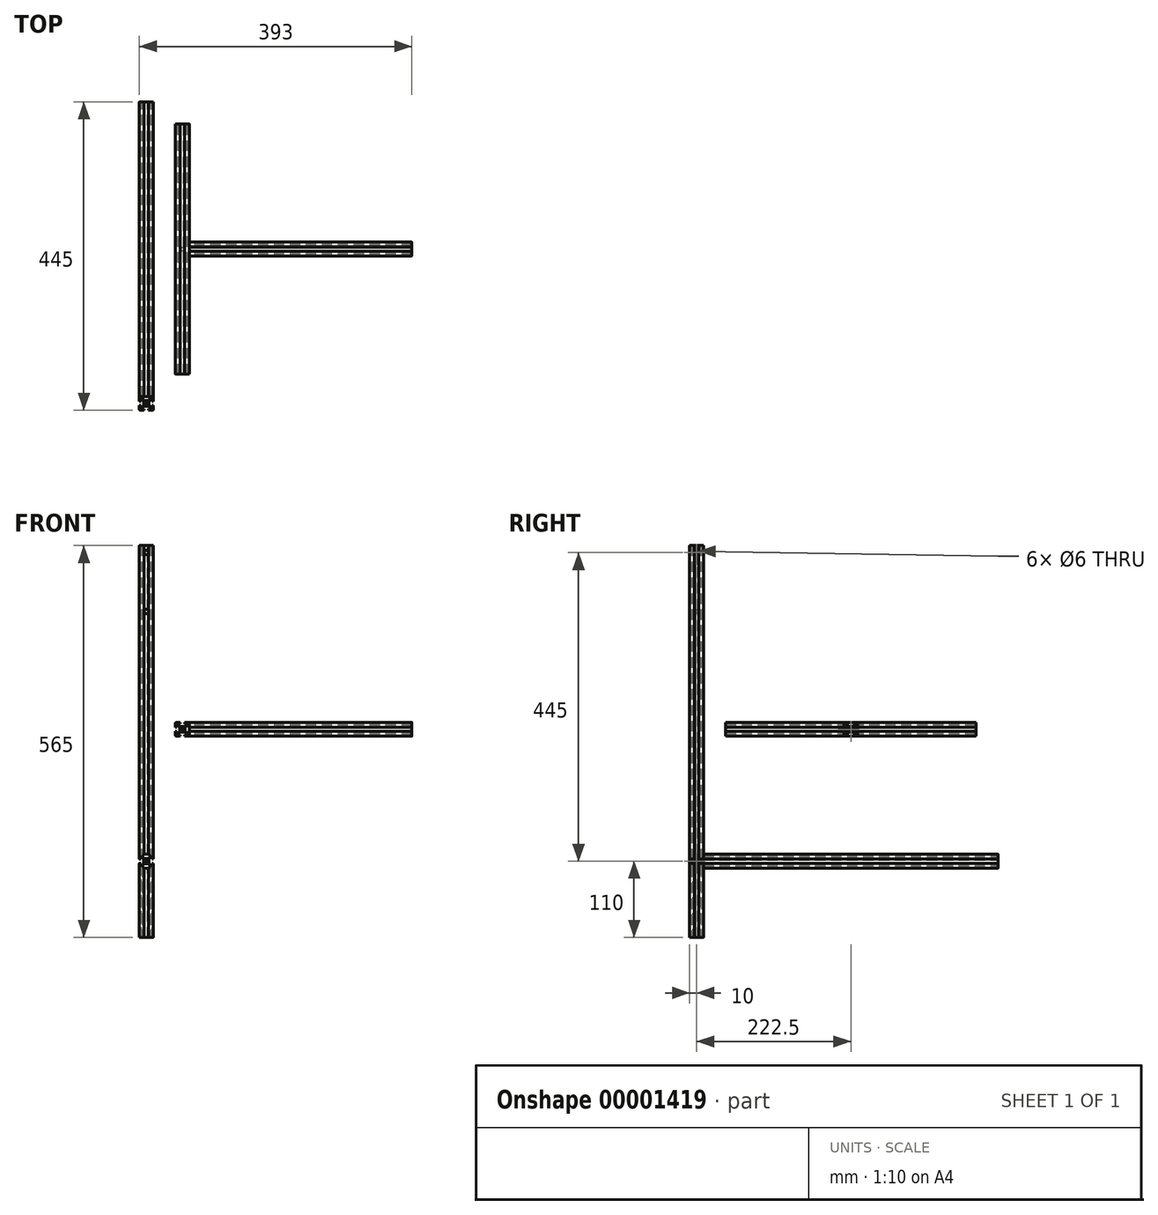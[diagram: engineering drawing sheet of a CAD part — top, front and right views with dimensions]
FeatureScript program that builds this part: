
annotation { "Feature Type Name" : "Feature", "Feature Type Description" : "" }
export const myFeature = defineFeature(function(context is Context, id is Id, definition is map)
    precondition{}
    {
        {
            var Q0;
            Q0=qCreatedBy(makeId("Top.planeOp"),FACE);
            cPlane(context, id + "F0", {"entities" : qUnion([Q0]), "cplaneType" : CPlaneType.OFFSET, "offset" : 565 * mm, "width" : 150 * mm, "height" : 150 * mm});
        }
        {
            var Q0;
            Q0=qCreatedBy(makeId("Top.planeOp"),FACE);
            var sketch = newSketch(context, id + "F1", { "sketchPlane" : qUnion([Q0])});
            skLineSegment(sketch, "E0", {"start": v(0, 0) * mm, "end": v(-232.5, 0) * mm, "construction": true});
            skLineSegment(sketch, "E1", {"start": v(0, 0) * mm, "end": v(0, -232.5) * mm, "construction": true});
            skLineSegment(sketch, "E2", {"start": v(0, -212.5) * mm, "end": v(-212.5, -212.5) * mm, "construction": true});
            skLineSegment(sketch, "E3", {"start": v(-212.5, -212.5) * mm, "end": v(-212.5, 0) * mm, "construction": true});
            skLineSegment(sketch, "E4", {"start": v(-232.5, 0) * mm, "end": v(-232.5, -212.5) * mm, "construction": true});
            skLineSegment(sketch, "E5", {"start": v(-232.5, -212.5) * mm, "end": v(-232.5, -232.5) * mm, "construction": true});
            skLineSegment(sketch, "E6", {"start": v(-232.5, -232.5) * mm, "end": v(-212.5, -232.5) * mm, "construction": true});
            skLineSegment(sketch, "E7", {"start": v(-212.5, -232.5) * mm, "end": v(0, -232.5) * mm, "construction": true});
            skLineSegment(sketch, "E8", {"start": v(-232.5, -212.5) * mm, "end": v(-212.5, -212.5) * mm, "construction": true});
            skLineSegment(sketch, "E9", {"start": v(-212.5, -232.5) * mm, "end": v(-212.5, -212.5) * mm, "construction": true});
            skLineSegment(sketch, "E10.0.MirrorCS", {"start": v(-212.5, 212.5) * mm, "end": v(-212.5, 0) * mm, "construction": true});
            skLineSegment(sketch, "E10.1.MirrorCS", {"start": v(-232.5, 0) * mm, "end": v(-232.5, 212.5) * mm, "construction": true});
            skLineSegment(sketch, "E10.2.MirrorCS", {"start": v(0, 212.5) * mm, "end": v(-212.5, 212.5) * mm, "construction": true});
            skLineSegment(sketch, "E10.3.MirrorCS", {"start": v(-212.5, 232.5) * mm, "end": v(0, 232.5) * mm, "construction": true});
            skLineSegment(sketch, "E10.4.MirrorCS", {"start": v(-232.5, 212.5) * mm, "end": v(-232.5, 232.5) * mm, "construction": true});
            skLineSegment(sketch, "E10.5.MirrorCS", {"start": v(-212.5, 232.5) * mm, "end": v(-212.5, 212.5) * mm, "construction": true});
            skLineSegment(sketch, "E10.6.MirrorCS", {"start": v(-232.5, 232.5) * mm, "end": v(-212.5, 232.5) * mm, "construction": true});
            skLineSegment(sketch, "E10.7.MirrorCS", {"start": v(-232.5, 212.5) * mm, "end": v(-212.5, 212.5) * mm, "construction": true});
            skLineSegment(sketch, "E11.0.MirrorCS", {"start": v(232.5, 232.5) * mm, "end": v(212.5, 232.5) * mm, "construction": true});
            skLineSegment(sketch, "E11.1.MirrorCS", {"start": v(232.5, 212.5) * mm, "end": v(232.5, 232.5) * mm, "construction": true});
            skLineSegment(sketch, "E11.2.MirrorCS", {"start": v(212.5, 232.5) * mm, "end": v(212.5, 212.5) * mm, "construction": true});
            skLineSegment(sketch, "E11.3.MirrorCS", {"start": v(232.5, 212.5) * mm, "end": v(212.5, 212.5) * mm, "construction": true});
            skLineSegment(sketch, "E11.4.MirrorCS", {"start": v(212.5, 232.5) * mm, "end": v(0, 232.5) * mm, "construction": true});
            skLineSegment(sketch, "E11.5.MirrorCS", {"start": v(0, 212.5) * mm, "end": v(212.5, 212.5) * mm, "construction": true});
            skLineSegment(sketch, "E11.6.MirrorCS", {"start": v(232.5, 0) * mm, "end": v(232.5, 212.5) * mm, "construction": true});
            skLineSegment(sketch, "E11.7.MirrorCS", {"start": v(212.5, 212.5) * mm, "end": v(212.5, 0) * mm, "construction": true});
            skLineSegment(sketch, "E11.8.MirrorCS", {"start": v(232.5, 0) * mm, "end": v(232.5, -212.5) * mm, "construction": true});
            skLineSegment(sketch, "E11.9.MirrorCS", {"start": v(212.5, -212.5) * mm, "end": v(212.5, 0) * mm, "construction": true});
            skLineSegment(sketch, "E11.10.MirrorCS", {"start": v(0, -212.5) * mm, "end": v(212.5, -212.5) * mm, "construction": true});
            skLineSegment(sketch, "E11.11.MirrorCS", {"start": v(212.5, -232.5) * mm, "end": v(0, -232.5) * mm, "construction": true});
            skLineSegment(sketch, "E11.12.MirrorCS", {"start": v(232.5, -232.5) * mm, "end": v(212.5, -232.5) * mm, "construction": true});
            skLineSegment(sketch, "E11.13.MirrorCS", {"start": v(232.5, -212.5) * mm, "end": v(232.5, -232.5) * mm, "construction": true});
            skLineSegment(sketch, "E11.14.MirrorCS", {"start": v(232.5, -212.5) * mm, "end": v(212.5, -212.5) * mm, "construction": true});
            skLineSegment(sketch, "E11.15.MirrorCS", {"start": v(212.5, -232.5) * mm, "end": v(212.5, -212.5) * mm, "construction": true});
            skLineSegment(sketch, "E12.0.MirrorCS", {"start": v(0, 0) * mm, "end": v(232.5, 0) * mm, "construction": true});
            skLineSegment(sketch, "E13.0.MirrorCS", {"start": v(0, 0) * mm, "end": v(0, 232.5) * mm, "construction": true});
            skSolve(sketch);
        }
        {
            var Q0;
            Q0=sQuery(id+"F1.wireOp",EDGE,"E13.0.MirrorCS");
            var Q1;
            Q1=sQuery(id+"F1.wireOp",VERTEX,"E10.2.MirrorCS.start");
            cPlane(context, id + "F2", {"entities" : qUnion([Q0, Q1]), "cplaneType" : CPlaneType.LINE_POINT, "offset" : 150 * mm, "width" : 150 * mm, "height" : 150 * mm});
        }
        {
            var Q0;
            Q0=qCreatedBy(makeId("Right.planeOp"),FACE);
            var sketch = newSketch(context, id + "F3", { "sketchPlane" : qUnion([Q0])});
            skLineSegment(sketch, "E14.rect.bottom", {"start": v(10, 10) * mm, "end": v(3, 10) * mm});
            skLineSegment(sketch, "E14.rect.top", {"start": v(10, -10) * mm, "end": v(3, -10) * mm});
            skLineSegment(sketch, "E14.rect.left", {"start": v(10, 10) * mm, "end": v(10, 3) * mm});
            skLineSegment(sketch, "E14.rect.right", {"start": v(-10, 10) * mm, "end": v(-10, 3) * mm});
            skPoint(sketch, "E14.rect.middle", {"position": v(0, 0) * mm});
            skLineSegment(sketch, "E15", {"start": v(-3, 10) * mm, "end": v(-3, 8) * mm});
            skLineSegment(sketch, "E16", {"start": v(-3, 8) * mm, "end": v(-6, 8) * mm});
            skLineSegment(sketch, "E17", {"start": v(-6, 8) * mm, "end": v(-6, 7.06) * mm});
            skLineSegment(sketch, "E18", {"start": v(-6, 7.06) * mm, "end": v(-2.94, 4) * mm});
            skLineSegment(sketch, "E19", {"start": v(-2.94, 4) * mm, "end": v(2.94, 4) * mm});
            skLineSegment(sketch, "E20", {"start": v(2.94, 4) * mm, "end": v(6, 7.06) * mm});
            skLineSegment(sketch, "E21", {"start": v(6, 7.06) * mm, "end": v(6, 8) * mm});
            skLineSegment(sketch, "E22", {"start": v(6, 8) * mm, "end": v(3, 8) * mm});
            skLineSegment(sketch, "E23", {"start": v(3, 8) * mm, "end": v(3, 10) * mm});
            skLineSegment(sketch, "E24.trimOffspring", {"start": v(-3, 10) * mm, "end": v(-10, 10) * mm});
            skLineSegment(sketch, "E25", {"start": v(10, 3) * mm, "end": v(8, 3) * mm});
            skLineSegment(sketch, "E26", {"start": v(8, 3) * mm, "end": v(8, 6) * mm});
            skLineSegment(sketch, "E27", {"start": v(8, 6) * mm, "end": v(7.06, 6) * mm});
            skLineSegment(sketch, "E28", {"start": v(7.06, 6) * mm, "end": v(4, 2.94) * mm});
            skLineSegment(sketch, "E29", {"start": v(4, 2.94) * mm, "end": v(4, -2.94) * mm});
            skLineSegment(sketch, "E30", {"start": v(4, -2.94) * mm, "end": v(7.06, -6) * mm});
            skLineSegment(sketch, "E31", {"start": v(7.06, -6) * mm, "end": v(8, -6) * mm});
            skLineSegment(sketch, "E32", {"start": v(8, -6) * mm, "end": v(8, -3) * mm});
            skLineSegment(sketch, "E33", {"start": v(8, -3) * mm, "end": v(10, -3) * mm});
            skLineSegment(sketch, "E34.trimOffspring", {"start": v(10, -3) * mm, "end": v(10, -10) * mm});
            skLineSegment(sketch, "E35", {"start": v(3, -10) * mm, "end": v(3, -8) * mm});
            skLineSegment(sketch, "E36", {"start": v(3, -8) * mm, "end": v(6, -8) * mm});
            skLineSegment(sketch, "E37", {"start": v(6, -8) * mm, "end": v(6, -7.06) * mm});
            skLineSegment(sketch, "E38", {"start": v(6, -7.06) * mm, "end": v(2.94, -4) * mm});
            skLineSegment(sketch, "E39", {"start": v(2.94, -4) * mm, "end": v(-2.94, -4) * mm});
            skLineSegment(sketch, "E40", {"start": v(-2.94, -4) * mm, "end": v(-6, -7.06) * mm});
            skLineSegment(sketch, "E41", {"start": v(-6, -7.06) * mm, "end": v(-6, -8) * mm});
            skLineSegment(sketch, "E42", {"start": v(-6, -8) * mm, "end": v(-3, -8) * mm});
            skLineSegment(sketch, "E43", {"start": v(-3, -8) * mm, "end": v(-3, -10) * mm});
            skLineSegment(sketch, "E44", {"start": v(-10, -3) * mm, "end": v(-8, -3) * mm});
            skLineSegment(sketch, "E45", {"start": v(-8, -3) * mm, "end": v(-8, -6) * mm});
            skLineSegment(sketch, "E46", {"start": v(-8, -6) * mm, "end": v(-7.06, -6) * mm});
            skLineSegment(sketch, "E47", {"start": v(-7.06, -6) * mm, "end": v(-4, -2.94) * mm});
            skLineSegment(sketch, "E48", {"start": v(-4, -2.94) * mm, "end": v(-4, 2.94) * mm});
            skLineSegment(sketch, "E49", {"start": v(-4, 2.94) * mm, "end": v(-7.06, 6) * mm});
            skLineSegment(sketch, "E50", {"start": v(-7.06, 6) * mm, "end": v(-8, 6) * mm});
            skLineSegment(sketch, "E51", {"start": v(-8, 6) * mm, "end": v(-8, 3) * mm});
            skLineSegment(sketch, "E52", {"start": v(-8, 3) * mm, "end": v(-10, 3) * mm});
            skLineSegment(sketch, "E53.trimOffspring", {"start": v(-3, -10) * mm, "end": v(-10, -10) * mm});
            skLineSegment(sketch, "E54.trimOffspring", {"start": v(-10, -3) * mm, "end": v(-10, -10) * mm});
            skSolve(sketch);
        }
        {
            var Q0;
            Q0=makeQuery(id+"F3.imprint","IMPRINT",FACE,{"disambiguationData":[TD([[makeQuery(id+"F3.imprint","IMPRINT",EDGE,{"derivedFrom":sQuery(id+"F3.wireOp",EDGE,"E14.rect.bottom")}),1.0]])]});
            extrude(context, id + "F4", {"entities" : qUnion([Q0]), "depth" : 321 * mm, "symmetric" : true});
        }
        {
            var Q0;
            Q0=makeQuery(id+"F4.opExtrude","CAP_FACE",FACE,{"disambiguationData":[OSD([sQuery(id+"F3.wireOp",EDGE,"E14.rect.bottom"),sQuery(id+"F3.wireOp",EDGE,"E14.rect.top"),sQuery(id+"F3.wireOp",EDGE,"E14.rect.left"),sQuery(id+"F3.wireOp",EDGE,"E14.rect.right"),sQuery(id+"F3.wireOp",EDGE,"E15"),sQuery(id+"F3.wireOp",EDGE,"E16"),sQuery(id+"F3.wireOp",EDGE,"E17"),sQuery(id+"F3.wireOp",EDGE,"E18"),sQuery(id+"F3.wireOp",EDGE,"E19"),sQuery(id+"F3.wireOp",EDGE,"E20"),sQuery(id+"F3.wireOp",EDGE,"E21"),sQuery(id+"F3.wireOp",EDGE,"E22"),sQuery(id+"F3.wireOp",EDGE,"E23"),sQuery(id+"F3.wireOp",EDGE,"E24.trimOffspring"),sQuery(id+"F3.wireOp",EDGE,"E25"),sQuery(id+"F3.wireOp",EDGE,"E26"),sQuery(id+"F3.wireOp",EDGE,"E27"),sQuery(id+"F3.wireOp",EDGE,"E28"),sQuery(id+"F3.wireOp",EDGE,"E29"),sQuery(id+"F3.wireOp",EDGE,"E30"),sQuery(id+"F3.wireOp",EDGE,"E31"),sQuery(id+"F3.wireOp",EDGE,"E32"),sQuery(id+"F3.wireOp",EDGE,"E33"),sQuery(id+"F3.wireOp",EDGE,"E34.trimOffspring"),sQuery(id+"F3.wireOp",EDGE,"E35"),sQuery(id+"F3.wireOp",EDGE,"E36"),sQuery(id+"F3.wireOp",EDGE,"E37"),sQuery(id+"F3.wireOp",EDGE,"E38"),sQuery(id+"F3.wireOp",EDGE,"E39"),sQuery(id+"F3.wireOp",EDGE,"E40"),sQuery(id+"F3.wireOp",EDGE,"E41"),sQuery(id+"F3.wireOp",EDGE,"E42"),sQuery(id+"F3.wireOp",EDGE,"E43"),sQuery(id+"F3.wireOp",EDGE,"E44"),sQuery(id+"F3.wireOp",EDGE,"E45"),sQuery(id+"F3.wireOp",EDGE,"E46"),sQuery(id+"F3.wireOp",EDGE,"E47"),sQuery(id+"F3.wireOp",EDGE,"E48"),sQuery(id+"F3.wireOp",EDGE,"E49"),sQuery(id+"F3.wireOp",EDGE,"E50"),sQuery(id+"F3.wireOp",EDGE,"E51"),sQuery(id+"F3.wireOp",EDGE,"E52"),sQuery(id+"F3.wireOp",EDGE,"E53.trimOffspring"),sQuery(id+"F3.wireOp",EDGE,"E54.trimOffspring")])],"isStart":false});
            var sketch = newSketch(context, id + "F5", { "sketchPlane" : qUnion([Q0])});
            skLineSegment(sketch, "E55", {"start": v(-4, 0) * mm, "end": v(4, 0) * mm, "construction": true});
            skCircle(sketch, "E56", {"center": v(0, 0) * mm, "radius": 2.1 * mm});
            skSolve(sketch);
        }
        {
            var Q0;
            Q0=makeQuery(id+"F5.imprint","IMPRINT",FACE,{"disambiguationData":[TD([[makeQuery(id+"F5.imprint","IMPRINT",EDGE,{"derivedFrom":sQuery(id+"F5.wireOp",EDGE,"E56")}),1.0]])]});
            extrude(context, id + "F6", {"entities" : qUnion([Q0]), "operationType" : NewBodyOperationType.REMOVE, "endBound" : BoundingType.THROUGH_ALL, "oppositeDirection" : true, "depth" : 25 * mm});
        }
        {
            var Q0;
            Q0=makeQuery(id+"F4.opExtrude","SWEPT_EDGE",EDGE,{"disambiguationData":[OSD([sQuery(id+"F3.wireOp",EDGE,"E14.rect.right"),sQuery(id+"F3.wireOp",EDGE,"E24.trimOffspring")])]});
            var Q1;
            Q1=makeQuery(id+"F4.opExtrude","SWEPT_EDGE",EDGE,{"disambiguationData":[OSD([sQuery(id+"F3.wireOp",EDGE,"E14.rect.bottom"),sQuery(id+"F3.wireOp",EDGE,"E14.rect.left")])]});
            var Q2;
            Q2=makeQuery(id+"F4.opExtrude","SWEPT_EDGE",EDGE,{"disambiguationData":[OSD([sQuery(id+"F3.wireOp",EDGE,"E53.trimOffspring"),sQuery(id+"F3.wireOp",EDGE,"E54.trimOffspring")])]});
            var Q3;
            Q3=makeQuery(id+"F4.opExtrude","SWEPT_EDGE",EDGE,{"disambiguationData":[OSD([sQuery(id+"F3.wireOp",EDGE,"E14.rect.top"),sQuery(id+"F3.wireOp",EDGE,"E34.trimOffspring")])]});
            fillet(context, id + "F7", {"entities" : qUnion([Q0, Q1, Q2, Q3]), "radius" : 1 * mm, "tangentPropagation" : true, "allowEdgeOverflow" : false});
        }
        {
            var Q0;
            Q0=qCreatedBy(makeId("Front.planeOp"),FACE);
            var sketch = newSketch(context, id + "F8", { "sketchPlane" : qUnion([Q0])});
            skLineSegment(sketch, "E57", {"start": v(-160.5, 10) * mm, "end": v(-160.5, 3) * mm});
            skLineSegment(sketch, "E58", {"start": v(-160.5, 3) * mm, "end": v(-162.5, 3) * mm});
            skLineSegment(sketch, "E59", {"start": v(-162.5, 3) * mm, "end": v(-162.5, 6) * mm});
            skLineSegment(sketch, "E60", {"start": v(-162.5, 6) * mm, "end": v(-163.44, 6) * mm});
            skLineSegment(sketch, "E61", {"start": v(-163.44, 6) * mm, "end": v(-166.5, 2.94) * mm});
            skLineSegment(sketch, "E62", {"start": v(-166.5, 2.94) * mm, "end": v(-166.5, -2.94) * mm});
            skLineSegment(sketch, "E63", {"start": v(-166.5, -2.94) * mm, "end": v(-163.44, -6) * mm});
            skLineSegment(sketch, "E64", {"start": v(-163.44, -6) * mm, "end": v(-162.5, -6) * mm});
            skLineSegment(sketch, "E65", {"start": v(-162.5, -6) * mm, "end": v(-162.5, -3) * mm});
            skLineSegment(sketch, "E66", {"start": v(-162.5, -3) * mm, "end": v(-160.5, -3) * mm});
            skLineSegment(sketch, "E67", {"start": v(-160.5, -3) * mm, "end": v(-160.5, -10) * mm});
            skLineSegment(sketch, "E68", {"start": v(-160.5, -10) * mm, "end": v(-167.5, -10) * mm});
            skLineSegment(sketch, "E69", {"start": v(-167.5, -10) * mm, "end": v(-167.5, -8) * mm});
            skLineSegment(sketch, "E70", {"start": v(-167.5, -8) * mm, "end": v(-164.5, -8) * mm});
            skLineSegment(sketch, "E71", {"start": v(-164.5, -8) * mm, "end": v(-164.5, -7.06) * mm});
            skLineSegment(sketch, "E72", {"start": v(-164.5, -7.06) * mm, "end": v(-167.56, -4) * mm});
            skLineSegment(sketch, "E73", {"start": v(-167.56, -4) * mm, "end": v(-173.44, -4) * mm});
            skLineSegment(sketch, "E74", {"start": v(-173.44, -4) * mm, "end": v(-176.5, -7.06) * mm});
            skLineSegment(sketch, "E75", {"start": v(-176.5, -7.06) * mm, "end": v(-176.5, -8) * mm});
            skLineSegment(sketch, "E76", {"start": v(-176.5, -8) * mm, "end": v(-173.5, -8) * mm});
            skLineSegment(sketch, "E77", {"start": v(-173.5, -8) * mm, "end": v(-173.5, -10) * mm});
            skLineSegment(sketch, "E78", {"start": v(-173.5, -10) * mm, "end": v(-180.5, -10) * mm});
            skLineSegment(sketch, "E79", {"start": v(-180.5, -10) * mm, "end": v(-180.5, -3) * mm});
            skLineSegment(sketch, "E80", {"start": v(-180.5, -3) * mm, "end": v(-178.5, -3) * mm});
            skLineSegment(sketch, "E81", {"start": v(-178.5, -3) * mm, "end": v(-178.5, -6) * mm});
            skLineSegment(sketch, "E82", {"start": v(-178.5, -6) * mm, "end": v(-177.56, -6) * mm});
            skLineSegment(sketch, "E83", {"start": v(-177.56, -6) * mm, "end": v(-174.5, -2.94) * mm});
            skLineSegment(sketch, "E84", {"start": v(-174.5, -2.94) * mm, "end": v(-174.5, 2.94) * mm});
            skLineSegment(sketch, "E85", {"start": v(-174.5, 2.94) * mm, "end": v(-177.56, 6) * mm});
            skLineSegment(sketch, "E86", {"start": v(-177.56, 6) * mm, "end": v(-178.5, 6) * mm});
            skLineSegment(sketch, "E87", {"start": v(-178.5, 6) * mm, "end": v(-178.5, 3) * mm});
            skLineSegment(sketch, "E88", {"start": v(-178.5, 3) * mm, "end": v(-180.5, 3) * mm});
            skLineSegment(sketch, "E89", {"start": v(-180.5, 3) * mm, "end": v(-180.5, 10) * mm});
            skLineSegment(sketch, "E90", {"start": v(-180.5, 10) * mm, "end": v(-173.5, 10) * mm});
            skLineSegment(sketch, "E91", {"start": v(-173.5, 10) * mm, "end": v(-173.5, 8) * mm});
            skLineSegment(sketch, "E92", {"start": v(-173.5, 8) * mm, "end": v(-176.5, 8) * mm});
            skLineSegment(sketch, "E93", {"start": v(-176.5, 8) * mm, "end": v(-176.5, 7.06) * mm});
            skLineSegment(sketch, "E94", {"start": v(-176.5, 7.06) * mm, "end": v(-173.44, 4) * mm});
            skLineSegment(sketch, "E95", {"start": v(-173.44, 4) * mm, "end": v(-167.56, 4) * mm});
            skLineSegment(sketch, "E96", {"start": v(-167.56, 4) * mm, "end": v(-164.5, 7.06) * mm});
            skLineSegment(sketch, "E97", {"start": v(-164.5, 7.06) * mm, "end": v(-164.5, 8) * mm});
            skLineSegment(sketch, "E98", {"start": v(-164.5, 8) * mm, "end": v(-167.5, 8) * mm});
            skLineSegment(sketch, "E99", {"start": v(-167.5, 8) * mm, "end": v(-167.5, 10) * mm});
            skLineSegment(sketch, "E100", {"start": v(-167.5, 10) * mm, "end": v(-160.5, 10) * mm});
            skLineSegment(sketch, "E101", {"start": v(-167.5, 10) * mm, "end": v(-173.5, 10) * mm, "construction": true});
            skLineSegment(sketch, "E102", {"start": v(-180.5, 3) * mm, "end": v(-180.5, -3) * mm, "construction": true});
            skLineSegment(sketch, "E103", {"start": v(-173.5, -10) * mm, "end": v(-167.5, -10) * mm, "construction": true});
            skLineSegment(sketch, "E104.0", {"start": v(160.5, 10) * mm, "end": v(-160.5, 10) * mm, "construction": true});
            skLineSegment(sketch, "E105.0", {"start": v(-160.5, -10) * mm, "end": v(160.5, -10) * mm, "construction": true});
            skLineSegment(sketch, "E106.0", {"start": v(160.5, -6) * mm, "end": v(-160.5, -6) * mm, "construction": true});
            skLineSegment(sketch, "E107", {"start": v(-160.5, -6) * mm, "end": v(-162.5, -6) * mm, "construction": true});
            skLineSegment(sketch, "E108.0", {"start": v(160.5, -8) * mm, "end": v(-160.5, -8) * mm, "construction": true});
            skLineSegment(sketch, "E109", {"start": v(-160.5, -8) * mm, "end": v(-164.5, -8) * mm, "construction": true});
            skLineSegment(sketch, "E110.0", {"start": v(160.5, -2.94) * mm, "end": v(-160.5, -2.94) * mm, "construction": true});
            skLineSegment(sketch, "E111", {"start": v(-160.5, -2.94) * mm, "end": v(-166.5, -2.94) * mm, "construction": true});
            skSolve(sketch);
        }
        {
            var Q0;
            Q0=makeQuery(id+"F8.imprint","IMPRINT",FACE,{"disambiguationData":[TD([[makeQuery(id+"F8.imprint","IMPRINT",EDGE,{"derivedFrom":sQuery(id+"F8.wireOp",EDGE,"E57")}),-1.0]])]});
            extrude(context, id + "F9", {"entities" : qUnion([Q0]), "depth" : 361 * mm, "symmetric" : true});
        }
        {
            var Q0;
            Q0=makeQuery(id+"F9.opExtrude","SWEPT_EDGE",EDGE,{"disambiguationData":[OSD([sQuery(id+"F8.wireOp",EDGE,"E89"),sQuery(id+"F8.wireOp",EDGE,"E90")])]});
            var Q1;
            Q1=makeQuery(id+"F9.opExtrude","SWEPT_EDGE",EDGE,{"disambiguationData":[OSD([sQuery(id+"F8.wireOp",EDGE,"E57"),sQuery(id+"F8.wireOp",EDGE,"E100")])]});
            var Q2;
            Q2=makeQuery(id+"F9.opExtrude","SWEPT_EDGE",EDGE,{"disambiguationData":[OSD([sQuery(id+"F8.wireOp",EDGE,"E78"),sQuery(id+"F8.wireOp",EDGE,"E79")])]});
            var Q3;
            Q3=makeQuery(id+"F9.opExtrude","SWEPT_EDGE",EDGE,{"disambiguationData":[OSD([sQuery(id+"F8.wireOp",EDGE,"E67"),sQuery(id+"F8.wireOp",EDGE,"E68")])]});
            fillet(context, id + "F10", {"entities" : qUnion([Q0, Q1, Q2, Q3]), "radius" : 1.5 * mm, "tangentPropagation" : true, "allowEdgeOverflow" : false});
        }
        {
            var Q0;
            Q0=makeQuery(id+"F9.opExtrude","CAP_FACE",FACE,{"disambiguationData":[OSD([sQuery(id+"F8.wireOp",EDGE,"E57"),sQuery(id+"F8.wireOp",EDGE,"E58"),sQuery(id+"F8.wireOp",EDGE,"E59"),sQuery(id+"F8.wireOp",EDGE,"E60"),sQuery(id+"F8.wireOp",EDGE,"E61"),sQuery(id+"F8.wireOp",EDGE,"E62"),sQuery(id+"F8.wireOp",EDGE,"E63"),sQuery(id+"F8.wireOp",EDGE,"E64"),sQuery(id+"F8.wireOp",EDGE,"E65"),sQuery(id+"F8.wireOp",EDGE,"E66"),sQuery(id+"F8.wireOp",EDGE,"E67"),sQuery(id+"F8.wireOp",EDGE,"E68"),sQuery(id+"F8.wireOp",EDGE,"E69"),sQuery(id+"F8.wireOp",EDGE,"E70"),sQuery(id+"F8.wireOp",EDGE,"E71"),sQuery(id+"F8.wireOp",EDGE,"E72"),sQuery(id+"F8.wireOp",EDGE,"E73"),sQuery(id+"F8.wireOp",EDGE,"E74"),sQuery(id+"F8.wireOp",EDGE,"E75"),sQuery(id+"F8.wireOp",EDGE,"E76"),sQuery(id+"F8.wireOp",EDGE,"E77"),sQuery(id+"F8.wireOp",EDGE,"E78"),sQuery(id+"F8.wireOp",EDGE,"E79"),sQuery(id+"F8.wireOp",EDGE,"E80"),sQuery(id+"F8.wireOp",EDGE,"E81"),sQuery(id+"F8.wireOp",EDGE,"E82"),sQuery(id+"F8.wireOp",EDGE,"E83"),sQuery(id+"F8.wireOp",EDGE,"E84"),sQuery(id+"F8.wireOp",EDGE,"E85"),sQuery(id+"F8.wireOp",EDGE,"E86"),sQuery(id+"F8.wireOp",EDGE,"E87"),sQuery(id+"F8.wireOp",EDGE,"E88"),sQuery(id+"F8.wireOp",EDGE,"E89"),sQuery(id+"F8.wireOp",EDGE,"E90"),sQuery(id+"F8.wireOp",EDGE,"E91"),sQuery(id+"F8.wireOp",EDGE,"E92"),sQuery(id+"F8.wireOp",EDGE,"E93"),sQuery(id+"F8.wireOp",EDGE,"E94"),sQuery(id+"F8.wireOp",EDGE,"E95"),sQuery(id+"F8.wireOp",EDGE,"E96"),sQuery(id+"F8.wireOp",EDGE,"E97"),sQuery(id+"F8.wireOp",EDGE,"E98"),sQuery(id+"F8.wireOp",EDGE,"E99"),sQuery(id+"F8.wireOp",EDGE,"E100")])],"isStart":true});
            var sketch = newSketch(context, id + "F11", { "sketchPlane" : qUnion([Q0])});
            skLineSegment(sketch, "E112", {"start": v(166.5, 0) * mm, "end": v(174.5, 0) * mm, "construction": true});
            skCircle(sketch, "E113", {"center": v(170.5, 0) * mm, "radius": 2.1 * mm});
            skSolve(sketch);
        }
        {
            var Q0;
            Q0=makeQuery(id+"F11.imprint","IMPRINT",FACE,{"disambiguationData":[TD([[makeQuery(id+"F11.imprint","IMPRINT",EDGE,{"derivedFrom":sQuery(id+"F11.wireOp",EDGE,"E113")}),1.0]])]});
            extrude(context, id + "F12", {"entities" : qUnion([Q0]), "operationType" : NewBodyOperationType.REMOVE, "endBound" : BoundingType.THROUGH_ALL, "oppositeDirection" : true, "depth" : 25 * mm});
        }
        {
            var Q0;
            Q0=makeQuery(id+"F9.opExtrude","SWEPT_FACE",FACE,{"disambiguationData":[OSD([sQuery(id+"F8.wireOp",EDGE,"E79")])]});
            var sketch = newSketch(context, id + "F13", { "sketchPlane" : qUnion([Q0])});
            skCircle(sketch, "E114.0", {"center": v(0, 0) * mm, "radius": 2.1 * mm, "construction": true});
            skCircle(sketch, "E115", {"center": v(0, 0) * mm, "radius": 3 * mm});
            skSolve(sketch);
        }
        {
            var Q0;
            Q0=makeQuery(id+"F13.imprint","IMPRINT",FACE,{"disambiguationData":[TD([[makeQuery(id+"F13.imprint","IMPRINT",EDGE,{"derivedFrom":sQuery(id+"F13.wireOp",EDGE,"E115")}),1.0]])]});
            extrude(context, id + "F14", {"entities" : qUnion([Q0]), "operationType" : NewBodyOperationType.REMOVE, "endBound" : BoundingType.THROUGH_ALL, "oppositeDirection" : true, "depth" : 25 * mm});
        }
        {
            var Q0;
            Q0=makeQuery(id+"F4.opExtrude","SWEPT_BODY",BODY,{"disambiguationData":[OSD([sQuery(id+"F3.wireOp",EDGE,"E14.rect.bottom"),sQuery(id+"F3.wireOp",EDGE,"E14.rect.top"),sQuery(id+"F3.wireOp",EDGE,"E14.rect.left"),sQuery(id+"F3.wireOp",EDGE,"E14.rect.right"),sQuery(id+"F3.wireOp",EDGE,"E15"),sQuery(id+"F3.wireOp",EDGE,"E16"),sQuery(id+"F3.wireOp",EDGE,"E17"),sQuery(id+"F3.wireOp",EDGE,"E18"),sQuery(id+"F3.wireOp",EDGE,"E19"),sQuery(id+"F3.wireOp",EDGE,"E20"),sQuery(id+"F3.wireOp",EDGE,"E21"),sQuery(id+"F3.wireOp",EDGE,"E22"),sQuery(id+"F3.wireOp",EDGE,"E23"),sQuery(id+"F3.wireOp",EDGE,"E24.trimOffspring"),sQuery(id+"F3.wireOp",EDGE,"E25"),sQuery(id+"F3.wireOp",EDGE,"E26"),sQuery(id+"F3.wireOp",EDGE,"E27"),sQuery(id+"F3.wireOp",EDGE,"E28"),sQuery(id+"F3.wireOp",EDGE,"E29"),sQuery(id+"F3.wireOp",EDGE,"E30"),sQuery(id+"F3.wireOp",EDGE,"E31"),sQuery(id+"F3.wireOp",EDGE,"E32"),sQuery(id+"F3.wireOp",EDGE,"E33"),sQuery(id+"F3.wireOp",EDGE,"E34.trimOffspring"),sQuery(id+"F3.wireOp",EDGE,"E35"),sQuery(id+"F3.wireOp",EDGE,"E36"),sQuery(id+"F3.wireOp",EDGE,"E37"),sQuery(id+"F3.wireOp",EDGE,"E38"),sQuery(id+"F3.wireOp",EDGE,"E39"),sQuery(id+"F3.wireOp",EDGE,"E40"),sQuery(id+"F3.wireOp",EDGE,"E41"),sQuery(id+"F3.wireOp",EDGE,"E42"),sQuery(id+"F3.wireOp",EDGE,"E43"),sQuery(id+"F3.wireOp",EDGE,"E44"),sQuery(id+"F3.wireOp",EDGE,"E45"),sQuery(id+"F3.wireOp",EDGE,"E46"),sQuery(id+"F3.wireOp",EDGE,"E47"),sQuery(id+"F3.wireOp",EDGE,"E48"),sQuery(id+"F3.wireOp",EDGE,"E49"),sQuery(id+"F3.wireOp",EDGE,"E50"),sQuery(id+"F3.wireOp",EDGE,"E51"),sQuery(id+"F3.wireOp",EDGE,"E52"),sQuery(id+"F3.wireOp",EDGE,"E53.trimOffspring"),sQuery(id+"F3.wireOp",EDGE,"E54.trimOffspring")])]});
            var Q1;
            Q1=makeQuery(id+"F9.opExtrude","SWEPT_BODY",BODY,{"disambiguationData":[OSD([sQuery(id+"F8.wireOp",EDGE,"E57"),sQuery(id+"F8.wireOp",EDGE,"E58"),sQuery(id+"F8.wireOp",EDGE,"E59"),sQuery(id+"F8.wireOp",EDGE,"E60"),sQuery(id+"F8.wireOp",EDGE,"E61"),sQuery(id+"F8.wireOp",EDGE,"E62"),sQuery(id+"F8.wireOp",EDGE,"E63"),sQuery(id+"F8.wireOp",EDGE,"E64"),sQuery(id+"F8.wireOp",EDGE,"E65"),sQuery(id+"F8.wireOp",EDGE,"E66"),sQuery(id+"F8.wireOp",EDGE,"E67"),sQuery(id+"F8.wireOp",EDGE,"E68"),sQuery(id+"F8.wireOp",EDGE,"E69"),sQuery(id+"F8.wireOp",EDGE,"E70"),sQuery(id+"F8.wireOp",EDGE,"E71"),sQuery(id+"F8.wireOp",EDGE,"E72"),sQuery(id+"F8.wireOp",EDGE,"E73"),sQuery(id+"F8.wireOp",EDGE,"E74"),sQuery(id+"F8.wireOp",EDGE,"E75"),sQuery(id+"F8.wireOp",EDGE,"E76"),sQuery(id+"F8.wireOp",EDGE,"E77"),sQuery(id+"F8.wireOp",EDGE,"E78"),sQuery(id+"F8.wireOp",EDGE,"E79"),sQuery(id+"F8.wireOp",EDGE,"E80"),sQuery(id+"F8.wireOp",EDGE,"E81"),sQuery(id+"F8.wireOp",EDGE,"E82"),sQuery(id+"F8.wireOp",EDGE,"E83"),sQuery(id+"F8.wireOp",EDGE,"E84"),sQuery(id+"F8.wireOp",EDGE,"E85"),sQuery(id+"F8.wireOp",EDGE,"E86"),sQuery(id+"F8.wireOp",EDGE,"E87"),sQuery(id+"F8.wireOp",EDGE,"E88"),sQuery(id+"F8.wireOp",EDGE,"E89"),sQuery(id+"F8.wireOp",EDGE,"E90"),sQuery(id+"F8.wireOp",EDGE,"E91"),sQuery(id+"F8.wireOp",EDGE,"E92"),sQuery(id+"F8.wireOp",EDGE,"E93"),sQuery(id+"F8.wireOp",EDGE,"E94"),sQuery(id+"F8.wireOp",EDGE,"E95"),sQuery(id+"F8.wireOp",EDGE,"E96"),sQuery(id+"F8.wireOp",EDGE,"E97"),sQuery(id+"F8.wireOp",EDGE,"E98"),sQuery(id+"F8.wireOp",EDGE,"E99"),sQuery(id+"F8.wireOp",EDGE,"E100")])]});
            var Q2;
            Q2=makeQuery(id+"FQTp1k7JhvyfgXn_2.opExtrude","SWEPT_BODY",BODY,{"disambiguationData":[OSD([sQuery(id+"FYqZYH6H5JORpV2_2.wireOp",EDGE,"1808a2ec-eaa2-4fec-ab40-e84c049e9c5d"),sQuery(id+"FYqZYH6H5JORpV2_2.wireOp",EDGE,"171b9b11-3871-4668-874c-b7a3fcd7bc47"),sQuery(id+"FYqZYH6H5JORpV2_2.wireOp",EDGE,"6f117bb8-1e0e-4dac-83b5-f96115e5fa81"),sQuery(id+"FYqZYH6H5JORpV2_2.wireOp",EDGE,"ae937f2c-14a7-42c1-89eb-57edcf7ad43a")])]});
            transform(context, id + "F15", {"entities" : qUnion([Q0, Q1, Q2]), "transformType" : TransformType.TRANSLATION_3D, "dx" : 0 * mm, "dy" : 0 * mm, "dz" : 300 * mm, "makeCopy" : false});
        }
        {
            var Q0;
            Q0=qCreatedBy(makeId("Top.planeOp"),FACE);
            var sketch = newSketch(context, id + "F16", { "sketchPlane" : qUnion([Q0])});
            skLineSegment(sketch, "E116.rect.bottom", {"start": v(-212.5, -232.5) * mm, "end": v(-219.5, -232.5) * mm});
            skLineSegment(sketch, "E116.rect.top", {"start": v(-212.5, -212.5) * mm, "end": v(-219.5, -212.5) * mm});
            skLineSegment(sketch, "E116.rect.left", {"start": v(-212.5, -232.5) * mm, "end": v(-212.5, -225.5) * mm});
            skLineSegment(sketch, "E116.rect.right", {"start": v(-232.5, -232.5) * mm, "end": v(-232.5, -225.5) * mm});
            skPoint(sketch, "E116.rect.middle", {"position": v(-222.5, -222.5) * mm});
            skLineSegment(sketch, "E117", {"start": v(-225.5, -212.5) * mm, "end": v(-225.5, -214.5) * mm});
            skLineSegment(sketch, "E118", {"start": v(-225.5, -214.5) * mm, "end": v(-228.5, -214.5) * mm});
            skLineSegment(sketch, "E119", {"start": v(-228.5, -214.5) * mm, "end": v(-228.5, -215.44) * mm});
            skLineSegment(sketch, "E120", {"start": v(-228.5, -215.44) * mm, "end": v(-225.44, -218.5) * mm});
            skLineSegment(sketch, "E121", {"start": v(-225.44, -218.5) * mm, "end": v(-219.56, -218.5) * mm});
            skLineSegment(sketch, "E122", {"start": v(-219.56, -218.5) * mm, "end": v(-216.5, -215.44) * mm});
            skLineSegment(sketch, "E123", {"start": v(-216.5, -215.44) * mm, "end": v(-216.5, -214.5) * mm});
            skLineSegment(sketch, "E124", {"start": v(-216.5, -214.5) * mm, "end": v(-219.5, -214.5) * mm});
            skLineSegment(sketch, "E125", {"start": v(-219.5, -214.5) * mm, "end": v(-219.5, -212.5) * mm});
            skLineSegment(sketch, "E126", {"start": v(-212.5, -219.5) * mm, "end": v(-214.5, -219.5) * mm});
            skLineSegment(sketch, "E127", {"start": v(-214.5, -219.5) * mm, "end": v(-214.5, -216.5) * mm});
            skLineSegment(sketch, "E128", {"start": v(-214.5, -216.5) * mm, "end": v(-215.44, -216.5) * mm});
            skLineSegment(sketch, "E129", {"start": v(-215.44, -216.5) * mm, "end": v(-218.5, -219.56) * mm});
            skLineSegment(sketch, "E130", {"start": v(-218.5, -219.56) * mm, "end": v(-218.5, -225.44) * mm});
            skLineSegment(sketch, "E131", {"start": v(-218.5, -225.44) * mm, "end": v(-215.44, -228.5) * mm});
            skLineSegment(sketch, "E132", {"start": v(-215.44, -228.5) * mm, "end": v(-214.5, -228.5) * mm});
            skLineSegment(sketch, "E133", {"start": v(-214.5, -228.5) * mm, "end": v(-214.5, -225.5) * mm});
            skLineSegment(sketch, "E134", {"start": v(-214.5, -225.5) * mm, "end": v(-212.5, -225.5) * mm});
            skLineSegment(sketch, "E135", {"start": v(-219.5, -232.5) * mm, "end": v(-219.5, -230.5) * mm});
            skLineSegment(sketch, "E136", {"start": v(-219.5, -230.5) * mm, "end": v(-216.5, -230.5) * mm});
            skLineSegment(sketch, "E137", {"start": v(-216.5, -230.5) * mm, "end": v(-216.5, -229.56) * mm});
            skLineSegment(sketch, "E138", {"start": v(-216.5, -229.56) * mm, "end": v(-219.56, -226.5) * mm});
            skLineSegment(sketch, "E139", {"start": v(-219.56, -226.5) * mm, "end": v(-225.44, -226.5) * mm});
            skLineSegment(sketch, "E140", {"start": v(-225.44, -226.5) * mm, "end": v(-228.5, -229.56) * mm});
            skLineSegment(sketch, "E141", {"start": v(-228.5, -229.56) * mm, "end": v(-228.5, -230.5) * mm});
            skLineSegment(sketch, "E142", {"start": v(-228.5, -230.5) * mm, "end": v(-225.5, -230.5) * mm});
            skLineSegment(sketch, "E143", {"start": v(-225.5, -230.5) * mm, "end": v(-225.5, -232.5) * mm});
            skLineSegment(sketch, "E144", {"start": v(-232.5, -219.5) * mm, "end": v(-230.5, -219.5) * mm});
            skLineSegment(sketch, "E145", {"start": v(-230.5, -219.5) * mm, "end": v(-230.5, -216.5) * mm});
            skLineSegment(sketch, "E146", {"start": v(-230.5, -216.5) * mm, "end": v(-229.56, -216.5) * mm});
            skLineSegment(sketch, "E147", {"start": v(-229.56, -216.5) * mm, "end": v(-226.5, -219.56) * mm});
            skLineSegment(sketch, "E148", {"start": v(-226.5, -219.56) * mm, "end": v(-226.5, -225.44) * mm});
            skLineSegment(sketch, "E149", {"start": v(-226.5, -225.44) * mm, "end": v(-229.56, -228.5) * mm});
            skLineSegment(sketch, "E150", {"start": v(-229.56, -228.5) * mm, "end": v(-230.5, -228.5) * mm});
            skLineSegment(sketch, "E151", {"start": v(-230.5, -228.5) * mm, "end": v(-230.5, -225.5) * mm});
            skLineSegment(sketch, "E152", {"start": v(-230.5, -225.5) * mm, "end": v(-232.5, -225.5) * mm});
            skLineSegment(sketch, "E153.trimOffspring", {"start": v(-232.5, -219.5) * mm, "end": v(-232.5, -212.5) * mm});
            skLineSegment(sketch, "E154.trimOffspring", {"start": v(-225.5, -212.5) * mm, "end": v(-232.5, -212.5) * mm});
            skLineSegment(sketch, "E155.trimOffspring", {"start": v(-212.5, -219.5) * mm, "end": v(-212.5, -212.5) * mm});
            skLineSegment(sketch, "E156.trimOffspring", {"start": v(-225.5, -232.5) * mm, "end": v(-232.5, -232.5) * mm});
            skSolve(sketch);
        }
        {
            var Q0;
            Q0=makeQuery(id+"F16.imprint","IMPRINT",FACE,{"disambiguationData":[TD([[makeQuery(id+"F16.imprint","IMPRINT",EDGE,{"derivedFrom":sQuery(id+"F16.wireOp",EDGE,"E116.rect.bottom")}),-1.0]])]});
            var Q1;
            Q1=qCreatedBy(id+"F0.planeOp",FACE);
            extrude(context, id + "F17", {"entities" : qUnion([Q0]), "endBound" : BoundingType.UP_TO_SURFACE, "endBoundEntityFace" : qUnion([Q1]), "depth" : 565 * mm});
        }
        {
            var Q0;
            Q0=makeQuery(id+"F17.opExtrude","SWEPT_EDGE",EDGE,{"disambiguationData":[OSD([sQuery(id+"F16.wireOp",EDGE,"E116.rect.bottom"),sQuery(id+"F16.wireOp",EDGE,"E116.rect.left")])]});
            var Q1;
            Q1=makeQuery(id+"F17.opExtrude","SWEPT_EDGE",EDGE,{"disambiguationData":[OSD([sQuery(id+"F16.wireOp",EDGE,"E116.rect.top"),sQuery(id+"F16.wireOp",EDGE,"E155.trimOffspring")])]});
            var Q2;
            Q2=makeQuery(id+"F17.opExtrude","SWEPT_EDGE",EDGE,{"disambiguationData":[OSD([sQuery(id+"F16.wireOp",EDGE,"E116.rect.right"),sQuery(id+"F16.wireOp",EDGE,"E156.trimOffspring")])]});
            var Q3;
            Q3=makeQuery(id+"F17.opExtrude","SWEPT_EDGE",EDGE,{"disambiguationData":[OSD([sQuery(id+"F16.wireOp",EDGE,"E153.trimOffspring"),sQuery(id+"F16.wireOp",EDGE,"E154.trimOffspring")])]});
            fillet(context, id + "F18", {"entities" : qUnion([Q0, Q1, Q2, Q3]), "radius" : 1 * mm, "tangentPropagation" : true, "allowEdgeOverflow" : false});
        }
        {
            var Q0;
            Q0=makeQuery(id+"F17.opExtrude","CAP_FACE",FACE,{"disambiguationData":[OSD([sQuery(id+"F16.wireOp",EDGE,"E116.rect.bottom"),sQuery(id+"F16.wireOp",EDGE,"E116.rect.top"),sQuery(id+"F16.wireOp",EDGE,"E116.rect.left"),sQuery(id+"F16.wireOp",EDGE,"E116.rect.right"),sQuery(id+"F16.wireOp",EDGE,"E117"),sQuery(id+"F16.wireOp",EDGE,"E118"),sQuery(id+"F16.wireOp",EDGE,"E119"),sQuery(id+"F16.wireOp",EDGE,"E120"),sQuery(id+"F16.wireOp",EDGE,"E121"),sQuery(id+"F16.wireOp",EDGE,"E122"),sQuery(id+"F16.wireOp",EDGE,"E123"),sQuery(id+"F16.wireOp",EDGE,"E124"),sQuery(id+"F16.wireOp",EDGE,"E125"),sQuery(id+"F16.wireOp",EDGE,"E126"),sQuery(id+"F16.wireOp",EDGE,"E127"),sQuery(id+"F16.wireOp",EDGE,"E128"),sQuery(id+"F16.wireOp",EDGE,"E129"),sQuery(id+"F16.wireOp",EDGE,"E130"),sQuery(id+"F16.wireOp",EDGE,"E131"),sQuery(id+"F16.wireOp",EDGE,"E132"),sQuery(id+"F16.wireOp",EDGE,"E133"),sQuery(id+"F16.wireOp",EDGE,"E134"),sQuery(id+"F16.wireOp",EDGE,"E135"),sQuery(id+"F16.wireOp",EDGE,"E136"),sQuery(id+"F16.wireOp",EDGE,"E137"),sQuery(id+"F16.wireOp",EDGE,"E138"),sQuery(id+"F16.wireOp",EDGE,"E139"),sQuery(id+"F16.wireOp",EDGE,"E140"),sQuery(id+"F16.wireOp",EDGE,"E141"),sQuery(id+"F16.wireOp",EDGE,"E142"),sQuery(id+"F16.wireOp",EDGE,"E143"),sQuery(id+"F16.wireOp",EDGE,"E144"),sQuery(id+"F16.wireOp",EDGE,"E145"),sQuery(id+"F16.wireOp",EDGE,"E146"),sQuery(id+"F16.wireOp",EDGE,"E147"),sQuery(id+"F16.wireOp",EDGE,"E148"),sQuery(id+"F16.wireOp",EDGE,"E149"),sQuery(id+"F16.wireOp",EDGE,"E150"),sQuery(id+"F16.wireOp",EDGE,"E151"),sQuery(id+"F16.wireOp",EDGE,"E152"),sQuery(id+"F16.wireOp",EDGE,"E153.trimOffspring"),sQuery(id+"F16.wireOp",EDGE,"E154.trimOffspring"),sQuery(id+"F16.wireOp",EDGE,"E155.trimOffspring"),sQuery(id+"F16.wireOp",EDGE,"E156.trimOffspring")])],"isStart":false});
            var sketch = newSketch(context, id + "F19", { "sketchPlane" : qUnion([Q0])});
            skLineSegment(sketch, "E157", {"start": v(-226.5, -222.5) * mm, "end": v(-218.5, -222.5) * mm, "construction": true});
            skCircle(sketch, "E158", {"center": v(-222.5, -222.5) * mm, "radius": 2.1 * mm});
            skSolve(sketch);
        }
        {
            var Q0;
            Q0=makeQuery(id+"F19.imprint","IMPRINT",FACE,{"disambiguationData":[TD([[makeQuery(id+"F19.imprint","IMPRINT",EDGE,{"derivedFrom":sQuery(id+"F19.wireOp",EDGE,"E158")}),1.0]])]});
            extrude(context, id + "F20", {"entities" : qUnion([Q0]), "operationType" : NewBodyOperationType.REMOVE, "endBound" : BoundingType.THROUGH_ALL, "oppositeDirection" : true, "depth" : 25 * mm});
        }
        {
            var Q0;
            Q0=makeQuery(id+"F17.opExtrude","SWEPT_FACE",FACE,{"disambiguationData":[OSD([sQuery(id+"F16.wireOp",EDGE,"E116.rect.bottom")])]});
            var sketch = newSketch(context, id + "F21", { "sketchPlane" : qUnion([Q0])});
            skLineSegment(sketch, "E159.0", {"start": v(-232.5, 0) * mm, "end": v(-232.5, 565) * mm, "construction": true});
            skLineSegment(sketch, "E160.0", {"start": v(-212.5, 565) * mm, "end": v(-212.5, 0) * mm, "construction": true});
            skLineSegment(sketch, "E161", {"start": v(-232.5, 565) * mm, "end": v(-222.5, 555) * mm, "construction": true});
            skLineSegment(sketch, "E162", {"start": v(-222.5, 555) * mm, "end": v(-212.5, 565) * mm, "construction": true});
            skCircle(sketch, "E163", {"center": v(-222.5, 555) * mm, "radius": 3 * mm});
            skLineSegment(sketch, "E164", {"start": v(-222.5, 555) * mm, "end": v(-222.5, 470) * mm, "construction": true});
            skCircle(sketch, "E165", {"center": v(-222.5, 470) * mm, "radius": 3 * mm});
            skLineSegment(sketch, "E166", {"start": v(-232.5, 0) * mm, "end": v(-212.5, 0) * mm, "construction": true});
            skLineSegment(sketch, "E167", {"start": v(-222.5, 0) * mm, "end": v(-222.5, 110) * mm, "construction": true});
            skCircle(sketch, "E168", {"center": v(-222.5, 110) * mm, "radius": 3 * mm});
            skSolve(sketch);
        }
        {
            var Q0;
            {Q0=qUnion([makeQuery(id+"F21.imprint","IMPRINT",FACE,{"disambiguationData":[TD([[makeQuery(id+"F21.imprint","IMPRINT",EDGE,{"derivedFrom":sQuery(id+"F21.wireOp",EDGE,"E163")}),1.0]])]}),makeQuery(id+"F21.imprint","IMPRINT",FACE,{"disambiguationData":[TD([[makeQuery(id+"F21.imprint","IMPRINT",EDGE,{"derivedFrom":sQuery(id+"F21.wireOp",EDGE,"E165")}),1.0]])]}),makeQuery(id+"F21.imprint","IMPRINT",FACE,{"disambiguationData":[TD([[makeQuery(id+"F21.imprint","IMPRINT",EDGE,{"derivedFrom":sQuery(id+"F21.wireOp",EDGE,"E168")}),1.0]])]})]);}
            extrude(context, id + "F22", {"entities" : qUnion([Q0]), "operationType" : NewBodyOperationType.REMOVE, "endBound" : BoundingType.THROUGH_ALL, "oppositeDirection" : true, "depth" : 25 * mm});
        }
        {
            var Q0;
            Q0=makeQuery(id+"F17.opExtrude","SWEPT_FACE",FACE,{"disambiguationData":[OSD([sQuery(id+"F16.wireOp",EDGE,"E154.trimOffspring")])]});
            var sketch = newSketch(context, id + "F23", { "sketchPlane" : qUnion([Q0])});
            skLineSegment(sketch, "E169.0", {"start": v(232.5, 0) * mm, "end": v(212.5, 0) * mm, "construction": true});
            skLineSegment(sketch, "E170", {"start": v(222.5, 0) * mm, "end": v(222.5, 110) * mm, "construction": true});
            skLineSegment(sketch, "E171.0", {"start": v(212.5, 0) * mm, "end": v(212.5, 565) * mm, "construction": true});
            skLineSegment(sketch, "E172.0", {"start": v(232.5, 565) * mm, "end": v(232.5, 0) * mm, "construction": true});
            skLineSegment(sketch, "E173.rect.bottom", {"start": v(232.5, 120) * mm, "end": v(212.5, 120) * mm});
            skLineSegment(sketch, "E173.rect.top", {"start": v(232.5, 100) * mm, "end": v(212.5, 100) * mm});
            skLineSegment(sketch, "E173.rect.left", {"start": v(232.5, 120) * mm, "end": v(232.5, 100) * mm});
            skLineSegment(sketch, "E173.rect.right", {"start": v(212.5, 120) * mm, "end": v(212.5, 100) * mm});
            skPoint(sketch, "E173.rect.middle", {"position": v(222.5, 110) * mm});
            skSolve(sketch);
        }
        {
            var Q0;
            {var subQ0=sQuery(id+"F16.wireOp",EDGE,"E154.trimOffspring");var subQ4=sQuery(id+"F23.wireOp",EDGE,"E173.rect.bottom");var subQ7=sQuery(id+"F23.wireOp",EDGE,"E173.rect.left");var subQ8=makeQuery(id+"F17.opExtrude","SWEPT_EDGE",EDGE,{"disambiguationData":[OSD([sQuery(id+"F16.wireOp",EDGE,"E117"),subQ0])]});var subQ10=makeQuery(id+"F23.imprint","INTERSECT",VERTEX,{"derivedFrom":[subQ8,subQ4]});var subQ12=sQuery(id+"F23.wireOp",EDGE,"E173.rect.right");Q0=qUnion([makeQuery(id+"F23.imprint","IMPRINT",FACE,{"disambiguationData":[TD([[makeQuery(id+"F23.imprint","IMPRINT",EDGE,{"derivedFrom":subQ7}),-1.0]])]}),makeQuery(id+"F23.imprint","IMPRINT",FACE,{"disambiguationData":[TD([[makeQuery(id+"F23.imprint","IMPRINT",EDGE,{"derivedFrom":subQ12}),1.0]])]}),makeQuery(id+"F23.imprint","IMPRINT",FACE,{"disambiguationData":[TD([[makeQuery(id+"F23.imprint","IMPRINT",EDGE,{"disambiguationData":[TD([[subQ10,1.0]])],"derivedFrom":subQ4}),1.0]])]})]);}
            var Q1;
            Q1=qCreatedBy(id+"F2.planeOp",FACE);
            extrude(context, id + "F24", {"entities" : qUnion([Q0]), "endBound" : BoundingType.UP_TO_SURFACE, "endBoundEntityFace" : qUnion([Q1]), "depth" : 25 * mm});
        }
        {
            var Q0;
            Q0=makeQuery(id+"F24.opExtrude","CAP_FACE",FACE,{"disambiguationData":[OSD([sQuery(id+"F23.wireOp",EDGE,"E173.rect.bottom"),sQuery(id+"F23.wireOp",EDGE,"E173.rect.top"),sQuery(id+"F23.wireOp",EDGE,"E173.rect.left"),sQuery(id+"F23.wireOp",EDGE,"E173.rect.right")])],"isStart":false});
            var sketch = newSketch(context, id + "F25", { "sketchPlane" : qUnion([Q0])});
            skLineSegment(sketch, "E174", {"start": v(212.5, 120) * mm, "end": v(232.5, 100) * mm, "construction": true});
            skCircle(sketch, "E175", {"center": v(222.5, 110) * mm, "radius": 2.1 * mm});
            skSolve(sketch);
        }
        {
            var Q0;
            Q0=makeQuery(id+"F25.imprint","IMPRINT",FACE,{"disambiguationData":[TD([[makeQuery(id+"F25.imprint","IMPRINT",EDGE,{"derivedFrom":sQuery(id+"F25.wireOp",EDGE,"E175")}),1.0]])]});
            extrude(context, id + "F26", {"entities" : qUnion([Q0]), "operationType" : NewBodyOperationType.REMOVE, "endBound" : BoundingType.THROUGH_ALL, "oppositeDirection" : true, "depth" : 25 * mm});
        }
        {
            var Q0;
            Q0=makeQuery(id+"F24.opExtrude","CAP_FACE",FACE,{"disambiguationData":[OSD([sQuery(id+"F23.wireOp",EDGE,"E173.rect.bottom"),sQuery(id+"F23.wireOp",EDGE,"E173.rect.top"),sQuery(id+"F23.wireOp",EDGE,"E173.rect.left"),sQuery(id+"F23.wireOp",EDGE,"E173.rect.right")])],"isStart":false});
            var sketch = newSketch(context, id + "F27", { "sketchPlane" : qUnion([Q0])});
            skLineSegment(sketch, "E176.0", {"start": v(219.5, 565) * mm, "end": v(219.5, 0) * mm, "construction": true});
            skLineSegment(sketch, "E177.0", {"start": v(225.5, 565) * mm, "end": v(225.5, 0) * mm, "construction": true});
            skLineSegment(sketch, "E178", {"start": v(219.5, 118) * mm, "end": v(216.5, 118) * mm});
            skLineSegment(sketch, "E179", {"start": v(216.5, 118) * mm, "end": v(216.5, 117.06) * mm});
            skLineSegment(sketch, "E180", {"start": v(228.5, 117.06) * mm, "end": v(228.5, 118) * mm});
            skLineSegment(sketch, "E181", {"start": v(228.5, 118) * mm, "end": v(225.5, 118) * mm});
            skLineSegment(sketch, "E182", {"start": v(225.5, 118) * mm, "end": v(225.5, 120) * mm});
            skLineSegment(sketch, "E183", {"start": v(225.5, 120) * mm, "end": v(219.5, 120) * mm});
            skLineSegment(sketch, "E184", {"start": v(219.5, 120) * mm, "end": v(219.5, 118) * mm});
            skLineSegment(sketch, "E185", {"start": v(216.5, 117.06) * mm, "end": v(219.56, 114) * mm});
            skLineSegment(sketch, "E186", {"start": v(219.56, 114) * mm, "end": v(225.44, 114) * mm});
            skLineSegment(sketch, "E187", {"start": v(225.44, 114) * mm, "end": v(228.5, 117.06) * mm});
            skLineSegment(sketch, "E188", {"start": v(232.5, 120) * mm, "end": v(212.5, 100) * mm, "construction": true});
            skLineSegment(sketch, "E189", {"start": v(212.5, 120) * mm, "end": v(232.5, 100) * mm, "construction": true});
            skLineSegment(sketch, "E190.0.MirrorCS", {"start": v(226.5, 107.06) * mm, "end": v(226.5, 112.94) * mm});
            skLineSegment(sketch, "E190.1.MirrorCS", {"start": v(232.5, 113) * mm, "end": v(232.5, 107) * mm});
            skLineSegment(sketch, "E190.2.MirrorCS", {"start": v(232.5, 107) * mm, "end": v(230.5, 107) * mm});
            skLineSegment(sketch, "E190.3.MirrorCS", {"start": v(230.5, 113) * mm, "end": v(232.5, 113) * mm});
            skLineSegment(sketch, "E190.4.MirrorCS", {"start": v(226.5, 112.94) * mm, "end": v(229.56, 116) * mm});
            skLineSegment(sketch, "E190.5.MirrorCS", {"start": v(230.5, 116) * mm, "end": v(230.5, 113) * mm});
            skLineSegment(sketch, "E190.6.MirrorCS", {"start": v(229.56, 104) * mm, "end": v(226.5, 107.06) * mm});
            skLineSegment(sketch, "E190.7.MirrorCS", {"start": v(229.56, 116) * mm, "end": v(230.5, 116) * mm});
            skLineSegment(sketch, "E190.8.MirrorCS", {"start": v(230.5, 107) * mm, "end": v(230.5, 104) * mm});
            skLineSegment(sketch, "E190.9.MirrorCS", {"start": v(230.5, 104) * mm, "end": v(229.56, 104) * mm});
            skLineSegment(sketch, "E191.0.MirrorCS", {"start": v(218.5, 107.06) * mm, "end": v(215.44, 104) * mm});
            skLineSegment(sketch, "E191.1.MirrorCS", {"start": v(216.5, 102.94) * mm, "end": v(216.5, 102) * mm});
            skLineSegment(sketch, "E191.2.MirrorCS", {"start": v(219.5, 102) * mm, "end": v(219.5, 100) * mm});
            skLineSegment(sketch, "E191.3.MirrorCS", {"start": v(214.5, 116) * mm, "end": v(215.44, 116) * mm});
            skLineSegment(sketch, "E191.4.MirrorCS", {"start": v(214.5, 107) * mm, "end": v(212.5, 107) * mm});
            skLineSegment(sketch, "E191.5.MirrorCS", {"start": v(212.5, 113) * mm, "end": v(214.5, 113) * mm});
            skLineSegment(sketch, "E191.6.MirrorCS", {"start": v(219.5, 100) * mm, "end": v(225.5, 100) * mm});
            skLineSegment(sketch, "E191.7.MirrorCS", {"start": v(225.44, 106) * mm, "end": v(219.56, 106) * mm});
            skLineSegment(sketch, "E191.8.MirrorCS", {"start": v(212.5, 107) * mm, "end": v(212.5, 113) * mm});
            skLineSegment(sketch, "E191.9.MirrorCS", {"start": v(218.5, 112.94) * mm, "end": v(218.5, 107.06) * mm});
            skLineSegment(sketch, "E191.10.MirrorCS", {"start": v(228.5, 102) * mm, "end": v(228.5, 102.94) * mm});
            skLineSegment(sketch, "E191.11.MirrorCS", {"start": v(214.5, 113) * mm, "end": v(214.5, 116) * mm});
            skLineSegment(sketch, "E191.12.MirrorCS", {"start": v(215.44, 104) * mm, "end": v(214.5, 104) * mm});
            skLineSegment(sketch, "E191.13.MirrorCS", {"start": v(225.5, 102) * mm, "end": v(228.5, 102) * mm});
            skLineSegment(sketch, "E191.14.MirrorCS", {"start": v(225.5, 100) * mm, "end": v(225.5, 102) * mm});
            skLineSegment(sketch, "E191.15.MirrorCS", {"start": v(228.5, 102.94) * mm, "end": v(225.44, 106) * mm});
            skLineSegment(sketch, "E191.16.MirrorCS", {"start": v(216.5, 102) * mm, "end": v(219.5, 102) * mm});
            skLineSegment(sketch, "E191.17.MirrorCS", {"start": v(219.56, 106) * mm, "end": v(216.5, 102.94) * mm});
            skLineSegment(sketch, "E191.18.MirrorCS", {"start": v(214.5, 104) * mm, "end": v(214.5, 107) * mm});
            skLineSegment(sketch, "E191.19.MirrorCS", {"start": v(215.44, 116) * mm, "end": v(218.5, 112.94) * mm});
            skSolve(sketch);
        }
        {
            var Q0;
            {Q0=qUnion([makeQuery(id+"F27.imprint","IMPRINT",FACE,{"disambiguationData":[TD([[makeQuery(id+"F27.imprint","IMPRINT",EDGE,{"derivedFrom":sQuery(id+"F27.wireOp",EDGE,"E178")}),1.0]])]}),makeQuery(id+"F27.imprint","IMPRINT",FACE,{"disambiguationData":[TD([[makeQuery(id+"F27.imprint","IMPRINT",EDGE,{"derivedFrom":sQuery(id+"F27.wireOp",EDGE,"E190.0.MirrorCS")}),-1.0]])]}),makeQuery(id+"F27.imprint","IMPRINT",FACE,{"disambiguationData":[TD([[makeQuery(id+"F27.imprint","IMPRINT",EDGE,{"derivedFrom":sQuery(id+"F27.wireOp",EDGE,"E191.0.MirrorCS")}),-1.0]])]}),makeQuery(id+"F27.imprint","IMPRINT",FACE,{"disambiguationData":[TD([[makeQuery(id+"F27.imprint","IMPRINT",EDGE,{"derivedFrom":sQuery(id+"F27.wireOp",EDGE,"E191.1.MirrorCS")}),1.0]])]})]);}
            extrude(context, id + "F28", {"entities" : qUnion([Q0]), "operationType" : NewBodyOperationType.REMOVE, "endBound" : BoundingType.THROUGH_ALL, "oppositeDirection" : true, "depth" : 25 * mm});
        }
        {
            var Q0;
            Q0=makeQuery(id+"F24.opExtrude","SWEPT_EDGE",EDGE,{"disambiguationData":[OSD([sQuery(id+"F23.wireOp",EDGE,"E173.rect.top"),sQuery(id+"F23.wireOp",EDGE,"E173.rect.right")])]});
            var Q1;
            Q1=makeQuery(id+"F24.opExtrude","SWEPT_EDGE",EDGE,{"disambiguationData":[OSD([sQuery(id+"F23.wireOp",EDGE,"E173.rect.bottom"),sQuery(id+"F23.wireOp",EDGE,"E173.rect.right")])]});
            var Q2;
            Q2=makeQuery(id+"F24.opExtrude","SWEPT_EDGE",EDGE,{"disambiguationData":[OSD([sQuery(id+"F23.wireOp",EDGE,"E173.rect.top"),sQuery(id+"F23.wireOp",EDGE,"E173.rect.left")])]});
            var Q3;
            Q3=makeQuery(id+"F24.opExtrude","SWEPT_EDGE",EDGE,{"disambiguationData":[OSD([sQuery(id+"F23.wireOp",EDGE,"E173.rect.bottom"),sQuery(id+"F23.wireOp",EDGE,"E173.rect.left")])]});
            fillet(context, id + "F29", {"entities" : qUnion([Q0, Q1, Q2, Q3]), "radius" : 1 * mm, "tangentPropagation" : true, "allowEdgeOverflow" : false});
        }
        {
            var Q0;
            Q0=makeQuery(id+"F17.opExtrude","SWEPT_FACE",FACE,{"disambiguationData":[OSD([sQuery(id+"F16.wireOp",EDGE,"E116.rect.right")])]});
            var sketch = newSketch(context, id + "F30", { "sketchPlane" : qUnion([Q0])});
            skLineSegment(sketch, "E192.0", {"start": v(232.5, 565) * mm, "end": v(232.5, 0) * mm, "construction": true});
            skLineSegment(sketch, "E192.1", {"start": v(212.5, 0) * mm, "end": v(212.5, 565) * mm, "construction": true});
            skLineSegment(sketch, "E193", {"start": v(212.5, 565) * mm, "end": v(222.5, 555) * mm, "construction": true});
            skLineSegment(sketch, "E194", {"start": v(222.5, 555) * mm, "end": v(232.5, 565) * mm, "construction": true});
            skCircle(sketch, "E195", {"center": v(222.5, 555) * mm, "radius": 3 * mm});
            skLineSegment(sketch, "E196", {"start": v(212.5, 0) * mm, "end": v(232.5, 0) * mm, "construction": true});
            skLineSegment(sketch, "E197", {"start": v(222.5, 0) * mm, "end": v(222.5, 110) * mm, "construction": true});
            skCircle(sketch, "E198", {"center": v(222.5, 110) * mm, "radius": 3 * mm});
            skSolve(sketch);
        }
        {
            var Q0;
            {Q0=qUnion([makeQuery(id+"F30.imprint","IMPRINT",FACE,{"disambiguationData":[TD([[makeQuery(id+"F30.imprint","IMPRINT",EDGE,{"derivedFrom":sQuery(id+"F30.wireOp",EDGE,"E195")}),1.0]])]}),makeQuery(id+"F30.imprint","IMPRINT",FACE,{"disambiguationData":[TD([[makeQuery(id+"F30.imprint","IMPRINT",EDGE,{"derivedFrom":sQuery(id+"F30.wireOp",EDGE,"E198")}),1.0]])]})]);}
            extrude(context, id + "F31", {"entities" : qUnion([Q0]), "operationType" : NewBodyOperationType.REMOVE, "endBound" : BoundingType.THROUGH_ALL, "oppositeDirection" : true, "depth" : 25 * mm});
        }
    });
